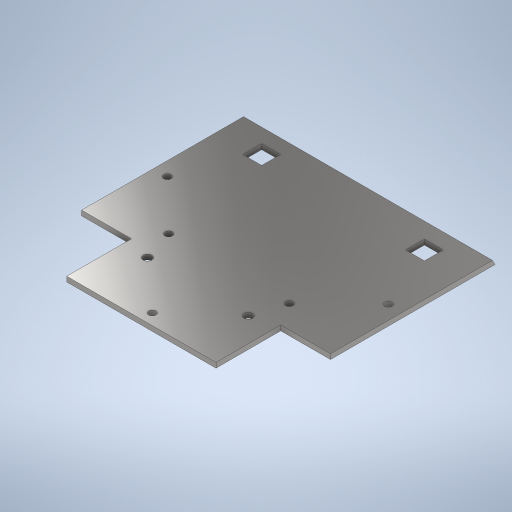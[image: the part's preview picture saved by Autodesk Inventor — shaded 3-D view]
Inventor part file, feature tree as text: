
AUTODESK INVENTOR PART (.ipt)
format: ipt  version: 2023 (Build 270158000, 158)  size: 286,720 bytes
history: native  units: mm
features: reference x13, other x8, extrude x4, sketch x4, projected_geometry x1
ambient origin geometry x8: Origin, YZ Plane, XZ Plane, XY Plane, X Axis, Y Axis, Z Axis, Center Point
bodies: Body1 (feature_tree)
feature tree (30):
  other  "Bryła1"
  extrude  "Wyciągnięcie proste1"  Depth=2.0mm TaperAngle=0.0deg
  extrude  "Wyciągnięcie proste2"  Depth=2.0mm TaperAngle=0.0deg
  extrude  "Wyciągnięcie proste3"  TaperAngle=0.0deg  [1 undecoded]
  extrude  "Wyciągnięcie proste4"  Depth=7.5mm
  sketch  "Szkic1"
  sketch  "Szkic2"
  reference  "Odniesienie1"
  reference  "Odniesienie2"
  reference  "Odniesienie3"
  reference  "Odniesienie4"
  sketch  "Szkic3"
  projected_geometry  "Pętla rzutowana1"
  reference  "Odniesienie5"
  sketch  "Szkic4"
  reference  "Odniesienie6"
  reference  "Odniesienie7"
  reference  "Odniesienie8"
  reference  "Odniesienie9"
  reference  "Odniesienie10"
  reference  "Odniesienie11"
  reference  "Odniesienie12"
  reference  "Odniesienie13"
  other  "<userpath>\Desktop\MojeRoboty\Stefan\mechanics 2\STEFAN.iam"
  other  "STEFAN.iam"
  other  "sciana_prawa_nowa:1"
  other  "sciana_prawa_nowa_MIR:1"
  other  "plug_2:1"
  other  "plytka_dol:1"
  other  "Board_1:1"
note: 1 required parameter value undecoded (feature->parameter linkage not recoverable at this tier; creation-order binding heuristic only, values carry confidence <= 0.55)
